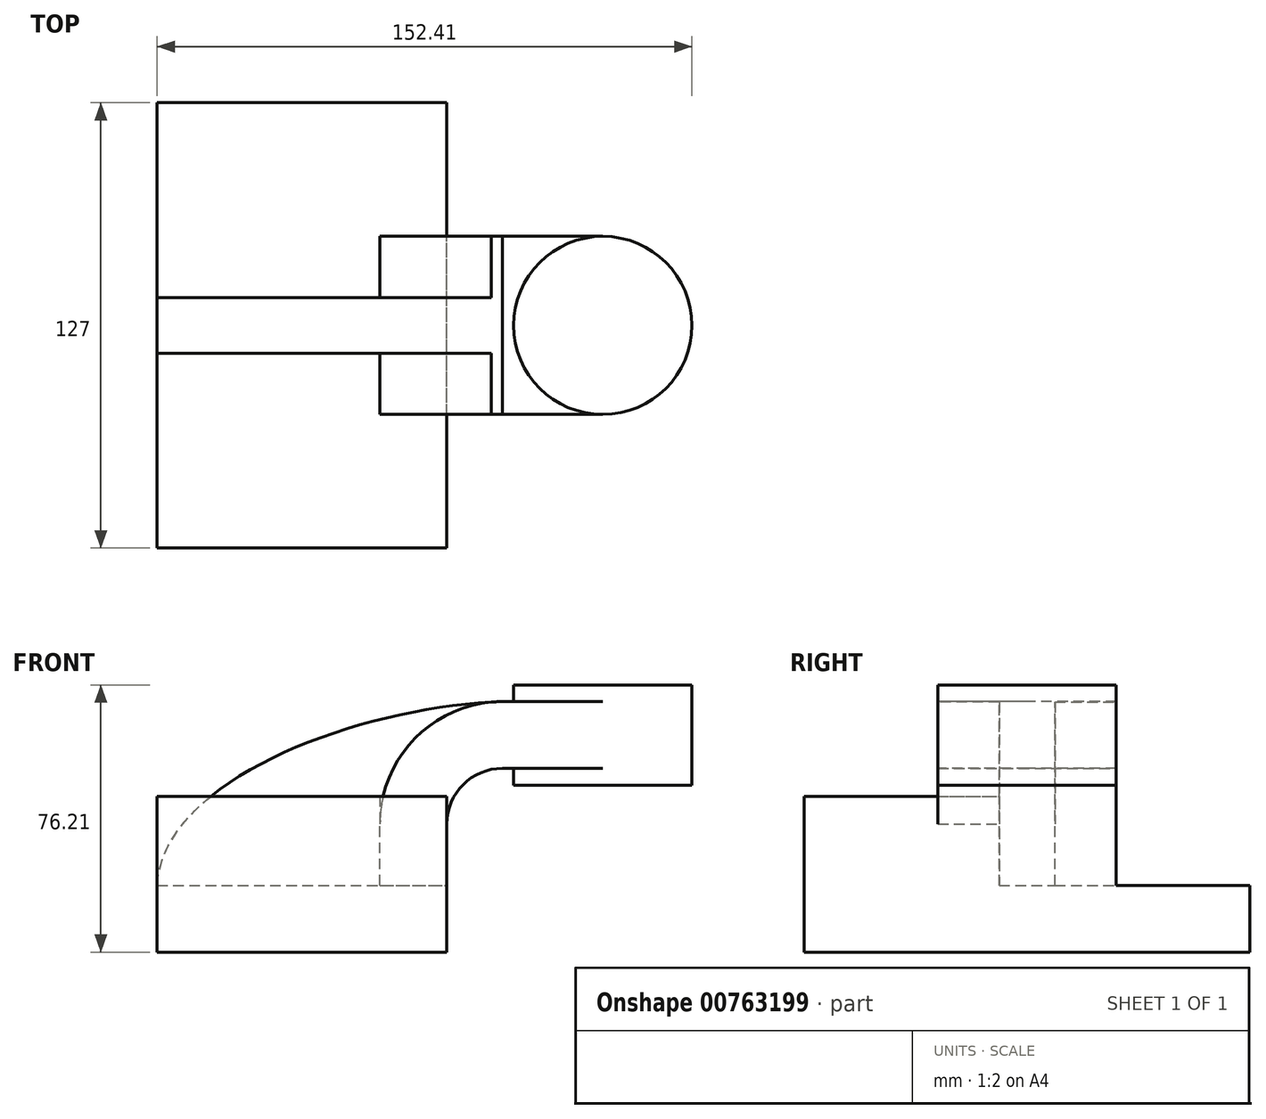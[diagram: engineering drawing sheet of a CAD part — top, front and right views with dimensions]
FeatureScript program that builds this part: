
annotation { "Feature Type Name" : "Feature", "Feature Type Description" : "" }
export const myFeature = defineFeature(function(context is Context, id is Id, definition is map)
    precondition{}
    {
        {
            var Q0;
            Q0=qCreatedBy(makeId("Front.planeOp"),FACE);
            var sketch = newSketch(context, id + "F0", { "sketchPlane" : qUnion([Q0])});
            skLineSegment(sketch, "E0.rect.bottom", {"start": v(-41.28, 9.52) * mm, "end": v(41.28, 9.52) * mm});
            skLineSegment(sketch, "E0.rect.top", {"start": v(-41.28, -9.52) * mm, "end": v(41.28, -9.52) * mm});
            skLineSegment(sketch, "E0.rect.left", {"start": v(-41.28, 9.52) * mm, "end": v(-41.28, -9.52) * mm});
            skLineSegment(sketch, "E0.rect.right", {"start": v(41.28, 9.52) * mm, "end": v(41.28, -9.52) * mm});
            skPoint(sketch, "E0.rect.middle", {"position": v(0, 0) * mm});
            skLineSegment(sketch, "E1", {"start": v(41.28, 9.52) * mm, "end": v(41.28, 27) * mm});
            skArc(sketch, "E2", {"start": v(41.28, 27) * mm, "mid": v(45.92, 38.23) * mm, "end": v(57.15, 42.88) * mm});
            skLineSegment(sketch, "E3", {"start": v(57.15, 42.88) * mm, "end": v(85.72, 42.88) * mm});
            skLineSegment(sketch, "E4.rect.bottom", {"start": v(60.32, 38.1) * mm, "end": v(111.12, 38.1) * mm});
            skLineSegment(sketch, "E4.rect.top", {"start": v(60.32, 66.68) * mm, "end": v(111.12, 66.68) * mm});
            skLineSegment(sketch, "E4.rect.left", {"start": v(60.32, 38.1) * mm, "end": v(60.32, 66.68) * mm});
            skLineSegment(sketch, "E4.rect.right", {"start": v(111.13, 38.1) * mm, "end": v(111.12, 66.68) * mm});
            skPoint(sketch, "E4.rect.middle", {"position": v(85.72, 52.39) * mm});
            skLineSegment(sketch, "E5.0", {"start": v(57.15, 61.93) * mm, "end": v(85.72, 61.93) * mm});
            skArc(sketch, "E5.1", {"start": v(22.23, 27) * mm, "mid": v(32.45, 51.7) * mm, "end": v(57.15, 61.93) * mm});
            skLineSegment(sketch, "E5.2", {"start": v(22.23, 9.52) * mm, "end": v(22.23, 27) * mm});
            skLineSegment(sketch, "E6", {"start": v(85.72, 38.1) * mm, "end": v(85.72, 66.68) * mm});
            skFitSpline(sketch, "E7", {"points": [v(-41.28, 9.53) * mm, v(57.15, 61.93) * mm], "startDerivative": vector(5.2, 92.34) * mm, "endDerivative": vector(120.92, 4.22) * mm});
            skSolve(sketch);
        }
        {
            var Q0;
            Q0=makeQuery(id+"F0.imprint","IMPRINT",FACE,{"disambiguationData":[TD([[makeQuery(id+"F0.imprint","IMPRINT",EDGE,{"derivedFrom":sQuery(id+"F0.wireOp",EDGE,"E0.rect.top")}),1.0]])]});
            extrude(context, id + "F1", {"entities" : qUnion([Q0]), "endBound" : BoundingType.SYMMETRIC, "depth" : 127 * mm});
        }
        {
            var Q0;
            {var subQ9=sQuery(id+"F0.wireOp",EDGE,"E1");Q0=makeQuery(id+"F0.imprint","IMPRINT",FACE,{"disambiguationData":[TD([[makeQuery(id+"F0.imprint","IMPRINT",EDGE,{"derivedFrom":subQ9}),1.0]])]});}
            var Q1;
            {var subQ0=sQuery(id+"F0.wireOp",EDGE,"E6");var subQ1=sQuery(id+"F0.wireOp",EDGE,"E3");var subQ2=makeQuery(id+"F0.imprint","INTERSECT",VERTEX,{"derivedFrom":[subQ1,subQ0]});Q1=makeQuery(id+"F0.imprint","IMPRINT",FACE,{"disambiguationData":[TD([[makeQuery(id+"F0.imprint","IMPRINT",EDGE,{"disambiguationData":[TD([[subQ2,1.0]])],"derivedFrom":subQ1}),1.0]])]});}
            extrude(context, id + "F2", {"entities" : qUnion([Q0, Q1]), "operationType" : NewBodyOperationType.ADD, "endBound" : BoundingType.SYMMETRIC, "depth" : 50.8 * mm});
        }
        {
            var Q0;
            {var subQ3=sQuery(id+"F0.wireOp",EDGE,"E5.2");Q0=makeQuery(id+"F0.imprint","IMPRINT",FACE,{"disambiguationData":[TD([[makeQuery(id+"F0.imprint","IMPRINT",EDGE,{"derivedFrom":subQ3}),1.0]])]});}
            extrude(context, id + "F3", {"entities" : qUnion([Q0]), "operationType" : NewBodyOperationType.ADD, "endBound" : BoundingType.SYMMETRIC, "depth" : 15.88 * mm});
        }
        {
            var Q0;
            {var subQ5=sQuery(id+"F0.wireOp",EDGE,"E4.rect.right");Q0=makeQuery(id+"F0.imprint","IMPRINT",FACE,{"disambiguationData":[TD([[makeQuery(id+"F0.imprint","IMPRINT",EDGE,{"derivedFrom":subQ5}),1.0]])]});}
            var Q1;
            Q1=sQuery(id+"F0.wireOp",EDGE,"E6");
            revolve(context, id + "F4", {"operationType" : NewBodyOperationType.ADD, "entities" : qUnion([Q0]), "axis" : qUnion([Q1]), "revolveType" : RevolveType.FULL});
        }
        {
            var Q0;
            {var subQ4=sQuery(id+"F0.wireOp",EDGE,"E0.rect.bottom");var subQ5=sQuery(id+"F0.wireOp",EDGE,"E0.rect.right");var subQ6=sQuery(id+"F0.wireOp",EDGE,"E0.rect.left");Q0=makeQuery(id+"F3.boolean.opBoolean","SPLIT",FACE,{"disambiguationData":[TD([makeQuery(id+"F1.opExtrude","CAP_FACE",FACE,{"disambiguationData":[OSD([subQ4,sQuery(id+"F0.wireOp",EDGE,"E0.rect.top"),subQ6,subQ5])],"isStart":false})])],"derivedFrom":makeQuery(id+"F1.opExtrude","SWEPT_FACE",FACE,{"disambiguationData":[OSD([subQ4])]})});}
            extrude(context, id + "F5", {"entities" : qUnion([Q0]), "operationType" : NewBodyOperationType.ADD, "depth" : 25.4 * mm, "offsetDistance" : 25.4 * mm});
        }
    });
